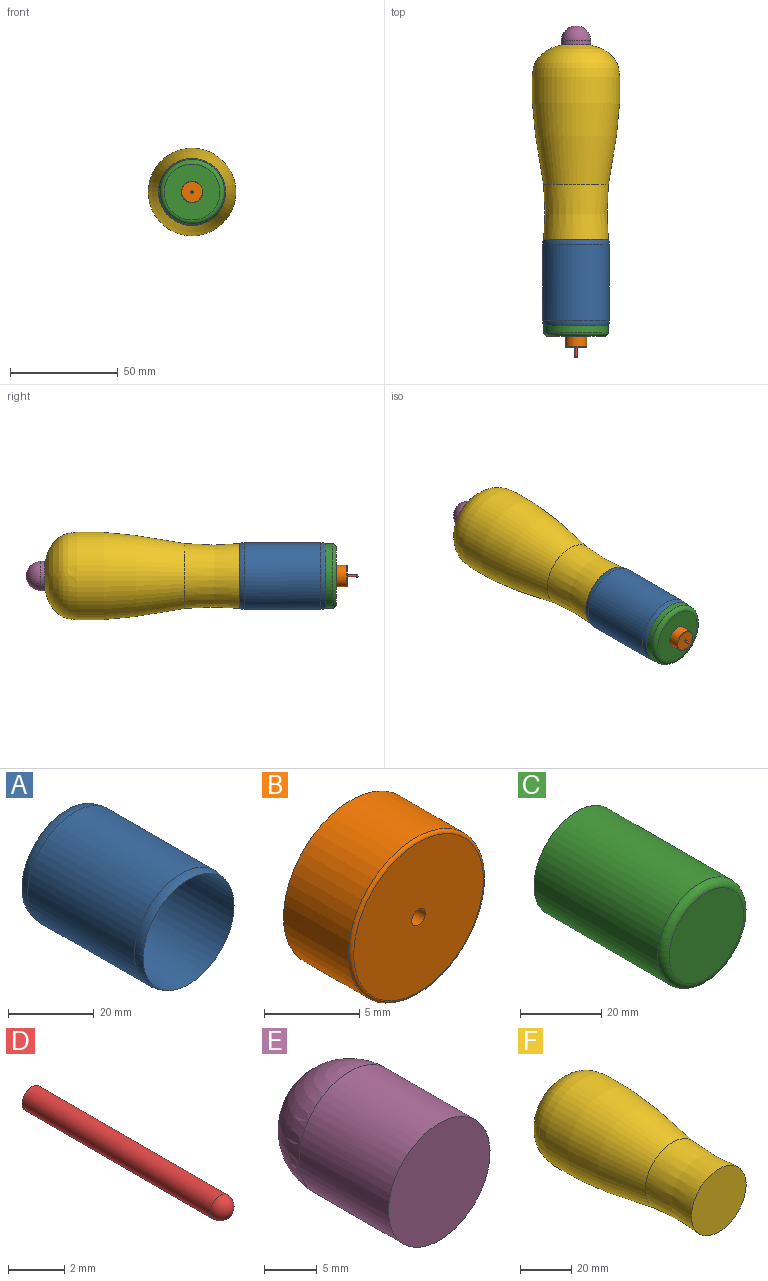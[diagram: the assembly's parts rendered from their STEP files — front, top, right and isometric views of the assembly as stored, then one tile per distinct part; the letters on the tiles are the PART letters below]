
ASSEMBLY  parts=6 mates=5
PART A: 4 faces, bbox 33.6x43.7x33.6 mm
  f0: cylinder r=15.5mm len=35.2mm, axis (0,1,0), area 3428.5mm2, adj f2,f3
  f1: cylinder r=15mm len=40mm, axis (0,-1,0), area 3769.9mm2, adj f2,f3
  f2: torus R=9.5mm, axis (0,-1,0), area 237.6mm2, adj f0,f1
  f3: torus R=9.5mm, axis (0,1,0), area 237.6mm2, adj f0,f1
PART B: 5 faces, bbox 10.8x5x10.8 mm
  f0: cylinder r=5mm len=10mm, axis (0,1,0), area 150.8mm2, adj f2,f4
  f1: plane 9.6x9.6mm, normal (0,-1,0), area 71.6mm2, adj f3,f4
  f2: plane 10x10mm, normal (0,1,0), area 77.8mm2, adj f0,f3
  f3: cylinder r=0.5mm len=5mm, axis (0,-1,0), area 15.7mm2, adj f1,f2
  f4: torus R=4.8mm, axis (0,-1,0), area 9.7mm2, adj f0,f1
PART C: 4 faces, bbox 32.4x45x32.4 mm
  f0: cylinder r=14.95mm len=43mm, axis (0,1,0), area 4039.1mm2, adj f2,f3
  f1: plane 25.9x25.9mm, normal (0,-1,0), area 526.9mm2, adj f3
  f2: plane 29.9x29.9mm, normal (0,1,0), area 702.2mm2, adj f0
  f3: torus R=12.95mm, axis (0,-1,0), area 280.8mm2, adj f0,f1
PART D: 3 faces, bbox 1x10x1 mm
  f0: cylinder r=0.5mm len=9.5mm, axis (0,1,0), area 29.8mm2, adj f1,f2
  f1: plane 1x1mm, normal (0,1,0), area 0.8mm2, adj f0
  f2: sphere r=0.5mm, area 1.6mm2, adj f0
PART E: 3 faces, bbox 13.6x18.8x13.6 mm
  f0: cylinder r=6.81mm len=13.62mm, axis (0,1,0), area 513.5mm2, adj f1,f2
  f1: plane 13.62x13.62mm, normal (0,-1,0), area 145.7mm2, adj f0
  f2: sphere r=6.81mm, area 291.4mm2, adj f0
PART F: 5 faces, bbox 40.8x90x40.8 mm
  f0: revolved ~64.62x40.81mm, area 7981.4mm2, adj f1,f3
  f1: revolved ~30x30mm, area 2333.1mm2, adj f0,f2
  f2: plane 30x30mm, normal (0,-1,0), area 706.9mm2, adj f1
  f3: cylinder r=6.81mm len=13.62mm, axis (0,1,0), area 428mm2, adj f0,f4
  f4: plane 13.62x13.62mm, normal (0,1,0), area 145.8mm2, adj f3
PLACE A t=(-45.91,-13.14,-2.48)mm
PLACE B t=(-45.91,-58.14,-2.48)mm
PLACE C t=(-45.91,-13.14,-2.48)mm
PLACE D t=(-45.91,-58.14,-2.48)mm
PLACE E t=(-45.91,78.86,-2.48)mm
PLACE F t=(-45.91,46.86,-2.48)mm
MATE fastened F.f3 <-> A.f1  axis (0,-1,0) through (-45.91,-13.14,-2.48)mm
MATE fastened E.f0 <-> F.f3  axis (0,-1,0) through (-45.91,66.86,-2.48)mm
MATE fastened B.f0 <-> C.f0  axis (0,1,0) through (-45.91,-58.14,-2.48)mm
MATE fastened C.f0 <-> F.f3  axis (0,1,0) through (-45.91,-13.14,-2.48)mm
MATE fastened D.f0 <-> B.f3  axis (0,1,0) through (-45.91,-58.14,-2.48)mm
